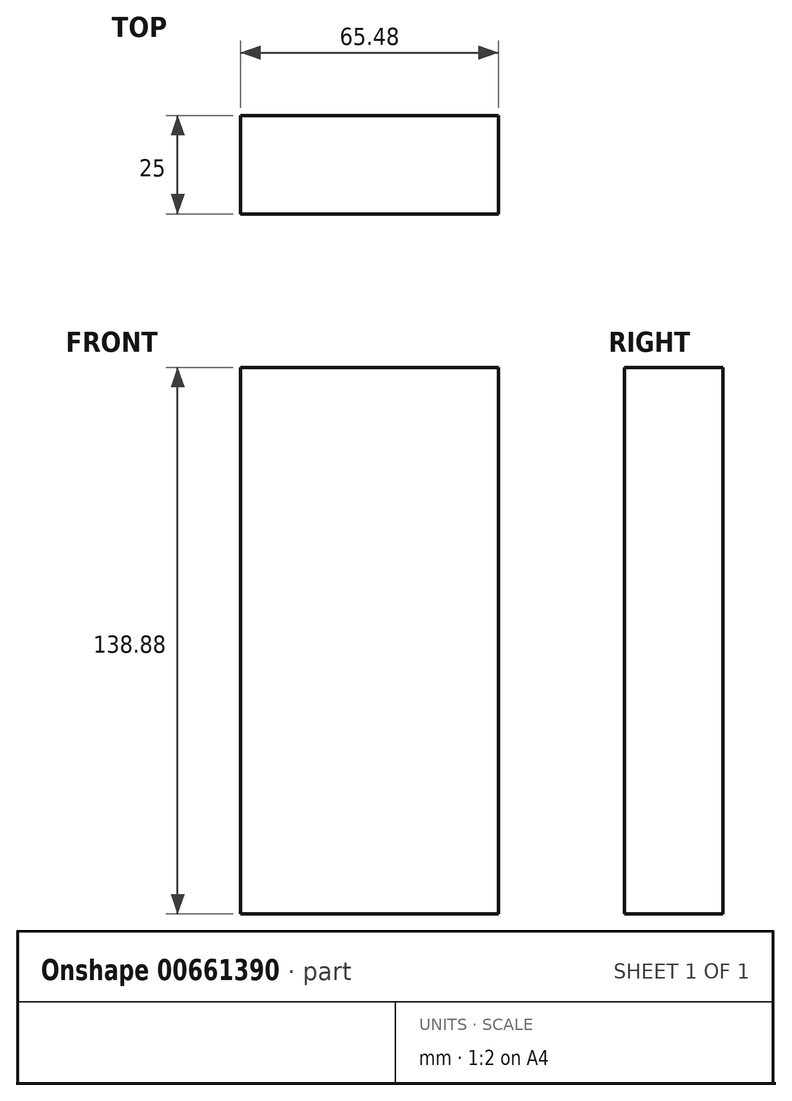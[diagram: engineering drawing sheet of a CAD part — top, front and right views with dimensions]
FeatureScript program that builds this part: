
annotation { "Feature Type Name" : "Feature", "Feature Type Description" : "" }
export const myFeature = defineFeature(function(context is Context, id is Id, definition is map)
    precondition{}
    {
        {
            var Q0;
            Q0=qCreatedBy(makeId("Front.planeOp"),FACE);
            var sketch = newSketch(context, id + "F0", { "sketchPlane" : qUnion([Q0])});
            skLineSegment(sketch, "E0.bottom", {"start": v(32.74, -69.44) * mm, "end": v(-32.74, -69.44) * mm});
            skLineSegment(sketch, "E0.top", {"start": v(32.74, 69.44) * mm, "end": v(-32.74, 69.44) * mm});
            skLineSegment(sketch, "E0.left", {"start": v(32.74, -69.44) * mm, "end": v(32.74, 69.44) * mm});
            skLineSegment(sketch, "E0.right", {"start": v(-32.74, -69.44) * mm, "end": v(-32.74, 69.44) * mm});
            skPoint(sketch, "E0.middle", {"position": v(0, 0) * mm});
            skSolve(sketch);
        }
        {
            var Q0;
            Q0=makeQuery(id+"F0.imprint","IMPRINT",FACE,{"disambiguationData":[TD([[makeQuery(id+"F0.imprint","IMPRINT",EDGE,{"derivedFrom":sQuery(id+"F0.wireOp",EDGE,"E0.bottom")}),-1.0]])]});
            extrude(context, id + "F1", {"entities" : qUnion([Q0]), "depth" : 25 * mm, "offsetDistance" : 25 * mm});
        }
    });
